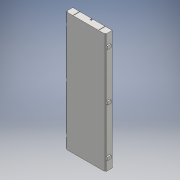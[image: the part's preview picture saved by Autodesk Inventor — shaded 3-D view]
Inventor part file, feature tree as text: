
AUTODESK INVENTOR PART (.ipt)
format: ipt  version: 2016 (Build 200138000, 138)  size: 4,220,928 bytes
history: native  units: mm
features: extrude x9, sketch x9, pattern_linear x6, projected_geometry x6, chamfer x2, fillet x1
ambient origin geometry x8: Origin, YZ Plane, XZ Plane, XY Plane, X Axis, Y Axis, Z Axis, Center Point
bodies: Solid1 (feature_tree)
feature tree (33):
  extrude  "Extrusion1"  Depth=166.0mm
  extrude  "Extrusion2"  Depth=27.5mm
  extrude  "Extrusion3"  Depth=3.0mm
  sketch  "Sketch6"  dims[d7=0.5mm d8=0.5mm]
  sketch  "Sketch7"  dims[d9=9.5mm d10=166.0mm d11=0.0mm]
  extrude  "Extrusion5"  Depth=0.5mm
  extrude  "Extrusion6"  Depth=166.0mm TaperAngle=0.0deg
  chamfer  "Chamfer3"  Distance=1.0mm
  pattern_linear  "Rectangular Pattern1"  Spacing1=2.0mm  [1 undecoded]
  chamfer  "Chamfer4"  Distance=2.0mm
  pattern_linear  "Rectangular Pattern2"  Spacing1=0.8mm  [1 undecoded]
  pattern_linear  "Rectangular Pattern3"  Spacing1=2.0mm  [1 undecoded]
  pattern_linear  "Rectangular Pattern4"  Spacing1=2.0mm  [1 undecoded]
  pattern_linear  "Rectangular Pattern5"  Spacing1=2.0mm  [1 undecoded]
  pattern_linear  "Rectangular Pattern6"  Spacing1=2.0mm  [1 undecoded]
  extrude  "Extrusion7"  Depth=2.0mm
  extrude  "Extrusion8"  Depth=2.0mm
  fillet  "Fillet1"  Radius=0.8mm
  extrude  "Extrusion9"  Depth=0.8mm
  extrude  "Extrusion10"  Depth=0.8mm
  sketch  "Sketch1"  dims[d0=55.0mm d1=166.0mm]
  sketch  "Sketch3"  dims[d2=9.0mm d3=0.0mm d4=27.5mm]
  projected_geometry  "Projected Loop1"
  sketch  "Sketch4"  dims[d5=2.0mm d6=3.0mm]
  projected_geometry  "Projected Loop2"
  sketch  "Sketch8"  dims[d12=27.5mm]
  sketch  "Sketch9"  dims[d13=52.0mm d14=1.0mm d15=0.0mm]
  sketch  "Sketch10"  dims[d16=2.0mm]
  projected_geometry  "Projected Loop7"
  sketch  "Sketch11"  dims[d17=2.0mm d18=2.0mm d19=2.0mm d20=0.8mm d21=2.0mm d22=2.0mm d23=2.0mm d24=2.0mm d25=2.0mm d26=2.0mm d27=0.8mm d28=0.8mm d29=0.8mm d30=0.8mm d46=2.25mm d57=2.0mm d58=3.0mm d59=7.45mm d62=1.0mm d63=1.0mm d64=1.0mm d65=1.0mm d66=1.0mm d67=1.0mm d68=1.0mm d69=1.0mm d70=1.0mm d71=1.0mm d72=1.0mm d73=1.0mm d74=1.0mm d75=1.0mm d84=2.0mm d85=2.0mm d86=2.0mm d88=0.8mm d103=1.0mm d104=1.0mm d105=1.0mm d106=1.0mm d117=1.0mm d118=0.0mm d119=1.0mm d120=0.0mm d121=0.5mm d122=2.0mm d123=45.0deg d124=20.0mm d126=19.2mm d127=0.5mm d128=2.0mm d129=45.0deg d130=20.0mm d132=45.3mm d133=50.0mm d135=2.8mm d136=100.0mm d138=15.5mm d139=320.0mm d141=2.51mm d142=20.0mm d144=80.3mm d145=0.6mm d146=155.0mm d147=6.0mm d148=1.0mm d149=0.6mm d150=155.0mm d151=1.0mm d152=0.6mm d153=155.0mm d154=0.6mm d155=155.0mm d156=1.0mm d157=1.0mm d158=0.1mm d159=0.0mm d160=0.6mm d161=0.6mm d162=1.0mm d163=1.0mm d164=1.0mm d165=1.0mm d166=0.6mm d167=0.6mm d168=1.0mm d169=1.0mm d170=1.0mm d171=1.0mm d172=1.3mm d173=1.6mm d174=2.6mm d175=0.7mm d176=1.6mm d177=1.3mm d178=2.6mm d179=0.7mm d180=0.6mm d181=0.6mm d182=1.0mm d183=1.0mm d184=1.0mm d185=1.0mm d186=0.6mm d187=0.6mm d188=1.0mm d189=1.0mm d190=1.0mm d191=1.0mm d192=2.6mm d193=2.6mm d194=1.3mm d195=1.6mm d196=0.7mm d197=1.3mm d198=1.6mm d199=0.7mm d200=0.1mm d201=0.0mm d202=0.5mm d203=83.0mm d205=16.0mm d206=4.0mm d207=5.0mm d208=4.0mm d209=5.0mm d210=4.0mm d211=5.0mm d212=2.0mm d213=0.0mm d214=2.0mm d215=0.0mm]
  projected_geometry  "Projected Loop8"
  projected_geometry  "Projected Loop9"
  projected_geometry  "Projected Loop10"
note: 6 required parameter values undecoded (feature->parameter linkage not recoverable at this tier; creation-order binding heuristic only, values carry confidence <= 0.55)
